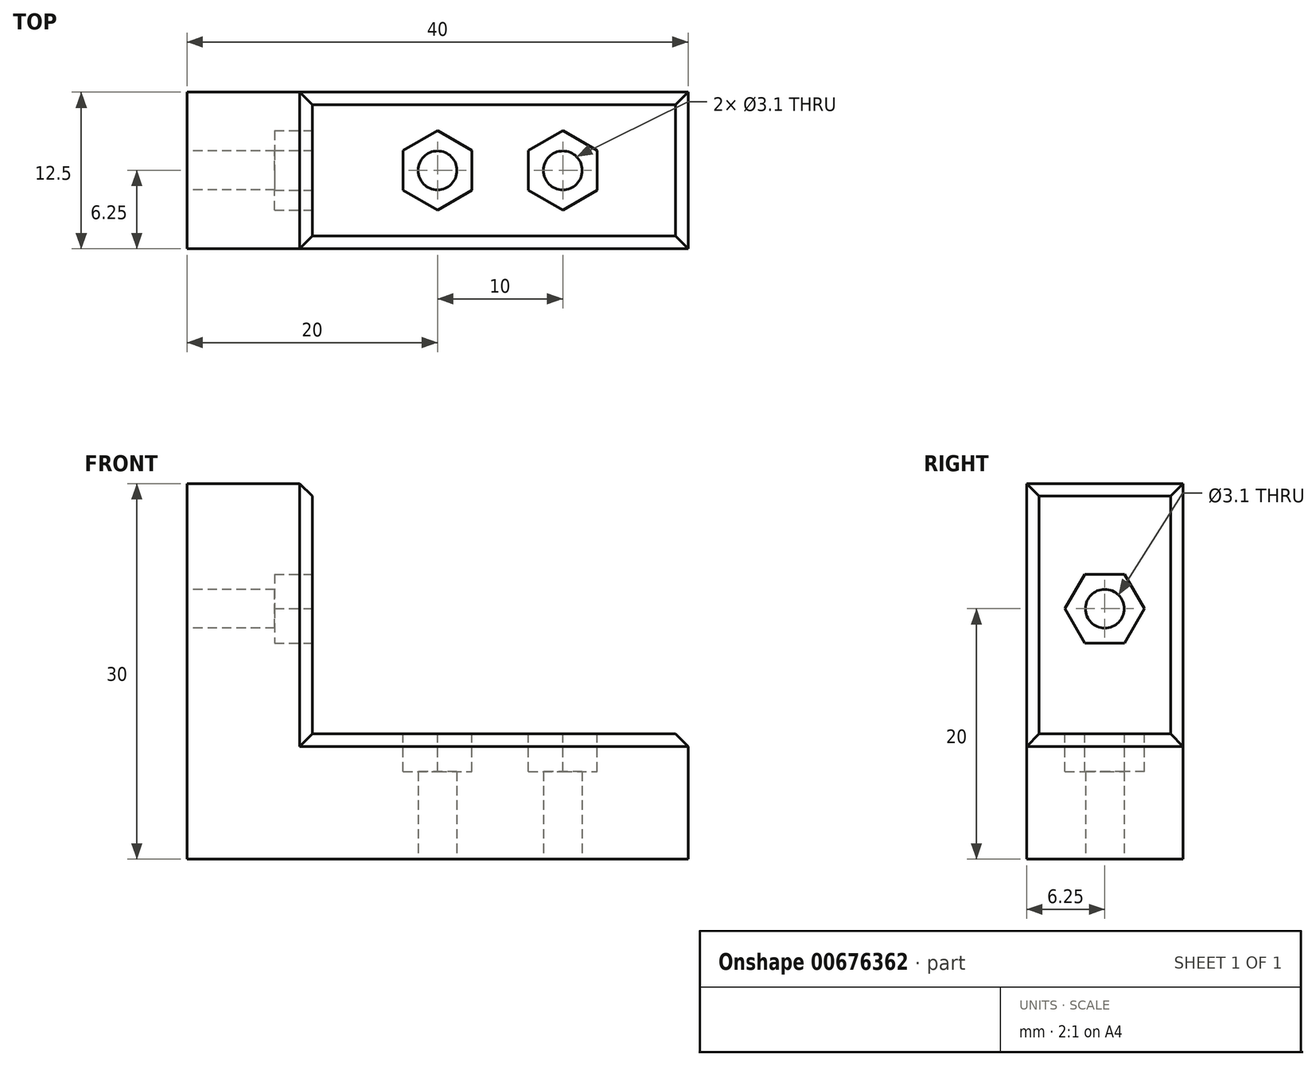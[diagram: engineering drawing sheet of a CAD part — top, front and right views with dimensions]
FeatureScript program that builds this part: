
annotation { "Feature Type Name" : "Feature", "Feature Type Description" : "" }
export const myFeature = defineFeature(function(context is Context, id is Id, definition is map)
    precondition{}
    {
        {
            var Q0;
            Q0=qCreatedBy(makeId("Top.planeOp"),FACE);
            var sketch = newSketch(context, id + "F0", { "sketchPlane" : qUnion([Q0])});
            skLineSegment(sketch, "E0", {"start": v(0, 0) * mm, "end": v(40, 0) * mm});
            skLineSegment(sketch, "E1", {"start": v(40, 0) * mm, "end": v(40, 12.5) * mm});
            skLineSegment(sketch, "E2", {"start": v(40, 12.5) * mm, "end": v(0, 12.5) * mm});
            skLineSegment(sketch, "E3", {"start": v(0, 12.5) * mm, "end": v(0, 0) * mm});
            skLineSegment(sketch, "E4", {"start": v(10, 12.5) * mm, "end": v(10, 0) * mm});
            skCircle(sketch, "E5", {"center": v(20, 6.25) * mm, "radius": 1.55 * mm});
            skPoint(sketch, "E5.centerSnap0", {"position": v(10, 6.25) * mm});
            skCircle(sketch, "E6", {"center": v(30, 6.25) * mm, "radius": 1.55 * mm});
            skSolve(sketch);
        }
        {
            var Q0;
            {var subQ1=sQuery(id+"F0.wireOp",EDGE,"E1");Q0=makeQuery(id+"F0.imprint","IMPRINT",FACE,{"disambiguationData":[TD([[makeQuery(id+"F0.imprint","IMPRINT",EDGE,{"derivedFrom":subQ1}),1.0]])]});}
            extrude(context, id + "F1", {"entities" : qUnion([Q0]), "depth" : 10 * mm, "offsetDistance" : 25 * mm});
        }
        {
            var Q0;
            {var subQ0=sQuery(id+"F0.wireOp",EDGE,"E3");Q0=makeQuery(id+"F0.imprint","IMPRINT",FACE,{"disambiguationData":[TD([[makeQuery(id+"F0.imprint","IMPRINT",EDGE,{"derivedFrom":subQ0}),1.0]])]});}
            extrude(context, id + "F2", {"entities" : qUnion([Q0]), "operationType" : NewBodyOperationType.ADD, "depth" : 30 * mm, "offsetDistance" : 25 * mm});
        }
        {
            var Q0;
            Q0=makeQuery(id+"F2.opExtrude","SWEPT_FACE",FACE,{"disambiguationData":[OSD([sQuery(id+"F0.wireOp",EDGE,"E3")])]});
            var sketch = newSketch(context, id + "F3", { "sketchPlane" : qUnion([Q0])});
            skCircle(sketch, "E7", {"center": v(-6.25, 20) * mm, "radius": 1.55 * mm});
            skPoint(sketch, "E7.centerSnap0", {"position": v(-6.25, 0) * mm});
            skSolve(sketch);
        }
        {
            var Q0;
            Q0=makeQuery(id+"F3.imprint","IMPRINT",FACE,{"disambiguationData":[TD([[makeQuery(id+"F3.imprint","IMPRINT",EDGE,{"derivedFrom":sQuery(id+"F3.wireOp",EDGE,"3LT1dNw4-eTpW-6s3u-LaV7-4F9vMbJp19KZ")}),1.0]])]});
            var Q1;
            Q1=makeQuery(id+"F3.imprint","IMPRINT",FACE,{"disambiguationData":[TD([[makeQuery(id+"F3.imprint","IMPRINT",EDGE,{"derivedFrom":sQuery(id+"F3.wireOp",EDGE,"E7")}),1.0]])]});
            extrude(context, id + "F4", {"entities" : qUnion([Q0, Q1]), "operationType" : NewBodyOperationType.REMOVE, "oppositeDirection" : true, "depth" : 10 * mm, "offsetDistance" : 25 * mm});
        }
        {
            var Q0;
            Q0=makeQuery(id+"F1.opExtrude","CAP_EDGE",EDGE,{"disambiguationData":[OSD([sQuery(id+"F0.wireOp",EDGE,"E0")])],"isStart":false});
            var Q1;
            Q1=makeQuery(id+"F1.opExtrude","CAP_EDGE",EDGE,{"disambiguationData":[OSD([sQuery(id+"F0.wireOp",EDGE,"E1")])],"isStart":false});
            var Q2;
            Q2=makeQuery(id+"F1.opExtrude","CAP_EDGE",EDGE,{"disambiguationData":[OSD([sQuery(id+"F0.wireOp",EDGE,"E2")])],"isStart":false});
            var Q3;
            Q3=makeQuery(id+"F2.opExtrude","SWEPT_EDGE",EDGE,{"disambiguationData":[OSD([sQuery(id+"F0.wireOp",EDGE,"E2"),sQuery(id+"F0.wireOp",EDGE,"E4")])]});
            var Q4;
            Q4=makeQuery(id+"F2.opExtrude","CAP_EDGE",EDGE,{"disambiguationData":[OSD([sQuery(id+"F0.wireOp",EDGE,"E4")])],"isStart":false});
            var Q5;
            Q5=makeQuery(id+"F2.opExtrude","SWEPT_EDGE",EDGE,{"disambiguationData":[OSD([sQuery(id+"F0.wireOp",EDGE,"E0"),sQuery(id+"F0.wireOp",EDGE,"E4")])]});
            chamfer(context, id + "F5", {"entities" : qUnion([Q0, Q1, Q2, Q3, Q4, Q5]), "width" : 1 * mm, "tangentPropagation" : true});
        }
        {
            var Q0;
            Q0=makeQuery(id+"F1.opExtrude","CAP_FACE",FACE,{"disambiguationData":[OSD([sQuery(id+"F0.wireOp",EDGE,"E0"),sQuery(id+"F0.wireOp",EDGE,"E1"),sQuery(id+"F0.wireOp",EDGE,"E2"),sQuery(id+"F0.wireOp",EDGE,"E4"),sQuery(id+"F0.wireOp",EDGE,"E5"),sQuery(id+"F0.wireOp",EDGE,"E6")])],"isStart":false});
            var sketch = newSketch(context, id + "F6", { "sketchPlane" : qUnion([Q0])});
            skCircle(sketch, "E8.cCircle", {"center": v(20, 6.25) * mm, "radius": 2.75 * mm, "construction": true});
            skLineSegment(sketch, "E8.0", {"start": v(22.75, 7.84) * mm, "end": v(22.75, 4.66) * mm});
            skLineSegment(sketch, "E8.1", {"start": v(22.75, 4.66) * mm, "end": v(20, 3.07) * mm});
            skLineSegment(sketch, "E8.2", {"start": v(20, 3.07) * mm, "end": v(17.25, 4.66) * mm});
            skLineSegment(sketch, "E8.3", {"start": v(17.25, 4.66) * mm, "end": v(17.25, 7.84) * mm});
            skLineSegment(sketch, "E8.4", {"start": v(17.25, 7.84) * mm, "end": v(20, 9.43) * mm});
            skLineSegment(sketch, "E8.5", {"start": v(20, 9.43) * mm, "end": v(22.75, 7.84) * mm});
            skPoint(sketch, "E8.0.midPoint", {"position": v(22.75, 6.25) * mm});
            skCircle(sketch, "E9.cCircle", {"center": v(30, 6.25) * mm, "radius": 2.75 * mm, "construction": true});
            skLineSegment(sketch, "E9.0", {"start": v(32.75, 7.84) * mm, "end": v(32.75, 4.66) * mm});
            skLineSegment(sketch, "E9.1", {"start": v(32.75, 4.66) * mm, "end": v(30, 3.07) * mm});
            skLineSegment(sketch, "E9.2", {"start": v(30, 3.07) * mm, "end": v(27.25, 4.66) * mm});
            skLineSegment(sketch, "E9.3", {"start": v(27.25, 4.66) * mm, "end": v(27.25, 7.84) * mm});
            skLineSegment(sketch, "E9.4", {"start": v(27.25, 7.84) * mm, "end": v(30, 9.43) * mm});
            skLineSegment(sketch, "E9.5", {"start": v(30, 9.43) * mm, "end": v(32.75, 7.84) * mm});
            skPoint(sketch, "E9.0.midPoint", {"position": v(32.75, 6.25) * mm});
            skSolve(sketch);
        }
        {
            var Q0;
            Q0 = qSketchRegion(id + "F6", true);
            extrude(context, id + "F7", {"entities" : qUnion([Q0]), "operationType" : NewBodyOperationType.REMOVE, "oppositeDirection" : true, "depth" : 3 * mm, "offsetDistance" : 25 * mm});
        }
        {
            var Q0;
            Q0=makeQuery(id+"F2.opExtrude","SWEPT_FACE",FACE,{"disambiguationData":[OSD([sQuery(id+"F0.wireOp",EDGE,"E4")])]});
            var sketch = newSketch(context, id + "F8", { "sketchPlane" : qUnion([Q0])});
            skCircle(sketch, "E10.cCircle", {"center": v(6.25, 20) * mm, "radius": 2.75 * mm, "construction": true});
            skLineSegment(sketch, "E10.0", {"start": v(7.84, 17.25) * mm, "end": v(4.66, 17.25) * mm});
            skLineSegment(sketch, "E10.1", {"start": v(4.66, 17.25) * mm, "end": v(3.07, 20) * mm});
            skLineSegment(sketch, "E10.2", {"start": v(3.07, 20) * mm, "end": v(4.66, 22.75) * mm});
            skLineSegment(sketch, "E10.3", {"start": v(4.66, 22.75) * mm, "end": v(7.84, 22.75) * mm});
            skLineSegment(sketch, "E10.4", {"start": v(7.84, 22.75) * mm, "end": v(9.43, 20) * mm});
            skLineSegment(sketch, "E10.5", {"start": v(9.43, 20) * mm, "end": v(7.84, 17.25) * mm});
            skPoint(sketch, "E10.0.midPoint", {"position": v(6.25, 17.25) * mm});
            skSolve(sketch);
        }
        {
            var Q0;
            Q0 = qSketchRegion(id + "F8", true);
            extrude(context, id + "F9", {"entities" : qUnion([Q0]), "operationType" : NewBodyOperationType.REMOVE, "oppositeDirection" : true, "depth" : 3 * mm, "offsetDistance" : 25 * mm});
        }
    });
